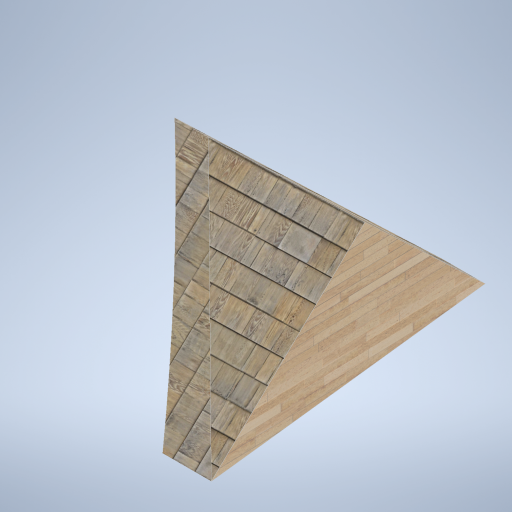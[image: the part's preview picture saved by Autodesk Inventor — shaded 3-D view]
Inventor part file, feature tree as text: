
AUTODESK INVENTOR PART (.ipt)
format: ipt  version: 2024.2 (Build 282272000, 272)  size: 520,704 bytes
history: native  units: mm
features: sketch x8, plane x6, extrude x3, loft x2, projected_geometry x2, other x1
ambient origin geometry x8: Origin, YZ Plane, XZ Plane, XY Plane, X Axis, Y Axis, Z Axis, Center Point
bodies: Solid1 (feature_tree)
feature tree (22):
  sketch  "Sketch1"  dims[d5=0.0mm d6=-7900.0mm d7=800.0mm]
  plane  "Work Plane2"
  loft  "Loft1"
  plane  "Work Plane3"
  extrude  "Extrusion1"  Depth=9000.0mm
  plane  "Work Plane4"
  sketch  "Sketch5"  dims[d12=800.0mm d13=0.0mm d14=90.0deg]
  plane  "Work Plane5"
  extrude  "Extrusion2"  Depth=9000.0mm
  plane  "Work Plane6"
  sketch  "Sketch7"  dims[d18=0.0mm d19=0.0mm]
  loft  "Loft2"
  extrude  "Extrusion3"  Depth=2500.0mm
  plane  "Work Plane1"
  sketch  "Sketch2"  dims[d8=9000.0mm d9=9000.0mm]
  sketch  "Sketch3"  dims[d10=9000.0mm d11=9000.0mm]
  sketch  "Sketch6"  dims[d15=0.0mm d16=90.0deg d17=2500.0mm]
  projected_geometry  "Projected Loop1"
  sketch  "Sketch8"  dims[d20=0.0mm]
  projected_geometry  "Projected Loop2"
  other  "Edges1"
  sketch  "Sketch9"  dims[d21=6.981317mm d22=0.0mm d23=0.0mm d24=90.0deg d25=0.0mm d26=90.0deg d27=0.0mm d28=90.0deg d29=1.0mm d30=0.0mm]
